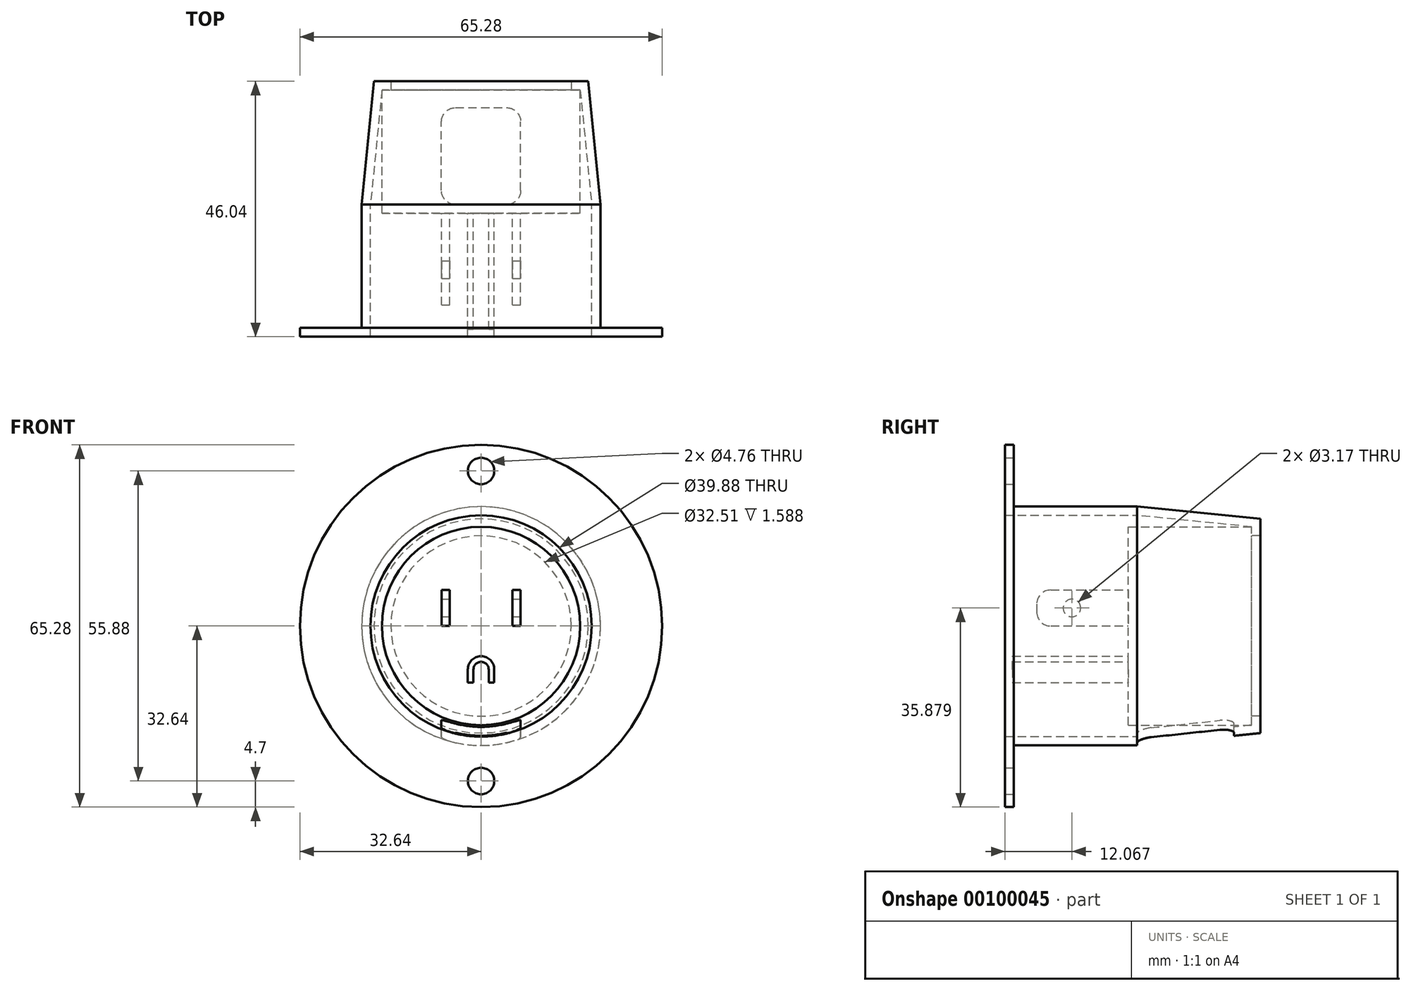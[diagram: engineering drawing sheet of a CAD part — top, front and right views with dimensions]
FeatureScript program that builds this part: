
annotation { "Feature Type Name" : "Feature", "Feature Type Description" : "" }
export const myFeature = defineFeature(function(context is Context, id is Id, definition is map)
    precondition{}
    {
        {
            var Q0;
            Q0=qCreatedBy(makeId("Front.planeOp"),FACE);
            var sketch = newSketch(context, id + "F0", { "sketchPlane" : qUnion([Q0])});
            skCircle(sketch, "E0", {"center": v(0, 0) * mm, "radius": 32.64 * mm});
            skCircle(sketch, "E1", {"center": v(0, 0) * mm, "radius": 19.94 * mm});
            skCircle(sketch, "E2", {"center": v(0, 27.94) * mm, "radius": 2.38 * mm});
            skCircle(sketch, "E3", {"center": v(0, -27.94) * mm, "radius": 2.38 * mm});
            skLineSegment(sketch, "E4", {"start": v(0, 27.94) * mm, "end": v(0, 0) * mm, "construction": true});
            skLineSegment(sketch, "E5", {"start": v(0, 0) * mm, "end": v(0, -27.94) * mm, "construction": true});
            skSolve(sketch);
        }
        {
            var Q0;
            Q0 = qSketchRegion(id + "F0", true);
            extrude(context, id + "F1", {"entities" : qUnion([Q0]), "depth" : 1.59 * mm});
        }
        {
            var Q0;
            Q0=qCreatedBy(makeId("Right.planeOp"),FACE);
            var sketch = newSketch(context, id + "F2", { "sketchPlane" : qUnion([Q0])});
            skLineSegment(sketch, "E6", {"start": v(0, 21.53) * mm, "end": v(22.23, 21.53) * mm});
            skLineSegment(sketch, "E7", {"start": v(22.22, 21.53) * mm, "end": v(44.45, 19.3) * mm});
            skLineSegment(sketch, "E8", {"start": v(44.45, 19.3) * mm, "end": v(44.45, 16.26) * mm});
            skLineSegment(sketch, "E9", {"start": v(42.86, 17.87) * mm, "end": v(22.15, 19.94) * mm});
            skLineSegment(sketch, "E10", {"start": v(22.15, 19.94) * mm, "end": v(0, 19.94) * mm});
            skLineSegment(sketch, "E11", {"start": v(0, 21.53) * mm, "end": v(0, 19.94) * mm});
            skLineSegment(sketch, "E12", {"start": v(0, 0) * mm, "end": v(44.45, 0) * mm, "construction": true});
            skLineSegment(sketch, "E13", {"start": v(11.11, 21.53) * mm, "end": v(11.11, 19.94) * mm, "construction": true});
            skLineSegment(sketch, "E14", {"start": v(42.86, 17.87) * mm, "end": v(43.02, 19.45) * mm, "construction": true});
            skLineSegment(sketch, "E15", {"start": v(42.86, 17.87) * mm, "end": v(42.86, 16.26) * mm});
            skLineSegment(sketch, "E16", {"start": v(42.86, 16.26) * mm, "end": v(44.45, 16.26) * mm});
            skSolve(sketch);
        }
        {
            var Q0;
            Q0 = qSketchRegion(id + "F2", true);
            var Q1;
            Q1=sQuery(id+"F2.wireOp",EDGE,"E12");
            revolve(context, id + "F3", {"operationType" : NewBodyOperationType.ADD, "entities" : qUnion([Q0]), "axis" : qUnion([Q1]), "revolveType" : RevolveType.FULL});
        }
        {
            var Q0;
            Q0=qCreatedBy(makeId("Top.planeOp"),FACE);
            var sketch = newSketch(context, id + "F4", { "sketchPlane" : qUnion([Q0])});
            skLineSegment(sketch, "E17.bottom", {"start": v(-7.14, 22.22) * mm, "end": v(7.14, 22.22) * mm});
            skLineSegment(sketch, "E17.top", {"start": v(-7.14, 39.69) * mm, "end": v(7.14, 39.69) * mm});
            skLineSegment(sketch, "E17.left", {"start": v(-7.14, 22.22) * mm, "end": v(-7.14, 39.69) * mm});
            skLineSegment(sketch, "E17.right", {"start": v(7.14, 22.22) * mm, "end": v(7.14, 39.69) * mm});
            skLineSegment(sketch, "E18", {"start": v(0, 22.22) * mm, "end": v(0, 0) * mm, "construction": true});
            skSolve(sketch);
        }
        {
            var Q0;
            Q0 = qSketchRegion(id + "F4", true);
            extrude(context, id + "F5", {"entities" : qUnion([Q0]), "operationType" : NewBodyOperationType.REMOVE, "oppositeDirection" : true, "depth" : 25.4 * mm});
        }
        {
            var Q0;
            Q0=makeQuery(id+"F5.boolean.opBoolean","COPY",EDGE,{"derivedFrom":makeQuery(id+"F5.opExtrude","SWEPT_EDGE",EDGE,{"disambiguationData":[OSD([sQuery(id+"F4.wireOp",EDGE,"E17.bottom"),sQuery(id+"F4.wireOp",EDGE,"E17.left")])]})});
            var Q1;
            Q1=makeQuery(id+"F5.boolean.opBoolean","COPY",EDGE,{"derivedFrom":makeQuery(id+"F5.opExtrude","SWEPT_EDGE",EDGE,{"disambiguationData":[OSD([sQuery(id+"F4.wireOp",EDGE,"E17.bottom"),sQuery(id+"F4.wireOp",EDGE,"E17.right")])]})});
            var Q2;
            Q2=makeQuery(id+"F5.boolean.opBoolean","COPY",EDGE,{"derivedFrom":makeQuery(id+"F5.opExtrude","SWEPT_EDGE",EDGE,{"disambiguationData":[OSD([sQuery(id+"F4.wireOp",EDGE,"E17.top"),sQuery(id+"F4.wireOp",EDGE,"E17.right")])]})});
            var Q3;
            Q3=makeQuery(id+"F5.boolean.opBoolean","COPY",EDGE,{"derivedFrom":makeQuery(id+"F5.opExtrude","SWEPT_EDGE",EDGE,{"disambiguationData":[OSD([sQuery(id+"F4.wireOp",EDGE,"E17.top"),sQuery(id+"F4.wireOp",EDGE,"E17.left")])]})});
            fillet(context, id + "F6", {"entities" : qUnion([Q0, Q1, Q2, Q3]), "radius" : 2.54 * mm, "tangentPropagation" : true, "allowEdgeOverflow" : false});
        }
        {
            var Q0;
            Q0=makeQuery(id+"F3.opRevolve","SWEPT_FACE",FACE,{"disambiguationData":[OSD([sQuery(id+"F2.wireOp",EDGE,"E15")])]});
            var sketch = newSketch(context, id + "F7", { "sketchPlane" : qUnion([Q0])});
            skCircle(sketch, "E19.0", {"center": v(0, 0) * mm, "radius": 17.87 * mm});
            skSolve(sketch);
        }
        {
            var Q0;
            Q0 = qSketchRegion(id + "F7", true);
            extrude(context, id + "F8", {"entities" : qUnion([Q0]), "operationType" : NewBodyOperationType.ADD, "depth" : 22.22 * mm});
        }
        {
            var Q0;
            Q0=makeQuery(id+"F8.opExtrude","CAP_FACE",FACE,{"disambiguationData":[OSD([sQuery(id+"F7.wireOp",EDGE,"E19.0")])],"isStart":false});
            var sketch = newSketch(context, id + "F9", { "sketchPlane" : qUnion([Q0])});
            skLineSegment(sketch, "E20.bottom", {"start": v(5.64, 6.48) * mm, "end": v(7.14, 6.48) * mm});
            skLineSegment(sketch, "E20.top", {"start": v(5.64, 0) * mm, "end": v(7.14, 0) * mm});
            skLineSegment(sketch, "E20.left", {"start": v(5.64, 6.48) * mm, "end": v(5.64, 0) * mm});
            skLineSegment(sketch, "E20.right", {"start": v(7.14, 6.48) * mm, "end": v(7.14, 0) * mm});
            skLineSegment(sketch, "E21.bottom", {"start": v(-7.14, 6.48) * mm, "end": v(-5.64, 6.48) * mm});
            skLineSegment(sketch, "E21.top", {"start": v(-7.14, 0) * mm, "end": v(-5.64, 0) * mm});
            skLineSegment(sketch, "E21.left", {"start": v(-7.14, 6.48) * mm, "end": v(-7.14, 0) * mm});
            skLineSegment(sketch, "E21.right", {"start": v(-5.64, 6.48) * mm, "end": v(-5.64, 0) * mm});
            skLineSegment(sketch, "E22.top", {"start": v(-2.38, -10.21) * mm, "end": v(-1.37, -10.21) * mm});
            skLineSegment(sketch, "E22.left", {"start": v(-2.38, -7.83) * mm, "end": v(-2.38, -10.21) * mm});
            skLineSegment(sketch, "E22.right", {"start": v(2.38, -7.83) * mm, "end": v(2.38, -10.21) * mm});
            skArc(sketch, "E23", {"start": v(2.38, -7.83) * mm, "mid": v(0, -5.45) * mm, "end": v(-2.38, -7.83) * mm});
            skLineSegment(sketch, "E24", {"start": v(-5.64, 3.24) * mm, "end": v(5.64, 3.24) * mm, "construction": true});
            skLineSegment(sketch, "E25", {"start": v(0, 3.24) * mm, "end": v(0, 0) * mm, "construction": true});
            skLineSegment(sketch, "E26.0", {"start": v(-1.37, -7.83) * mm, "end": v(-1.37, -10.21) * mm});
            skArc(sketch, "E26.1", {"start": v(1.37, -7.83) * mm, "mid": v(0, -6.46) * mm, "end": v(-1.37, -7.83) * mm});
            skLineSegment(sketch, "E26.2", {"start": v(1.37, -7.83) * mm, "end": v(1.37, -10.21) * mm});
            skLineSegment(sketch, "E27.trimOffspring", {"start": v(1.37, -10.21) * mm, "end": v(2.38, -10.21) * mm});
            skSolve(sketch);
        }
        {
            var Q0;
            Q0=makeQuery(id+"F9.imprint","IMPRINT",FACE,{"disambiguationData":[TD([[makeQuery(id+"F9.imprint","IMPRINT",EDGE,{"derivedFrom":sQuery(id+"F9.wireOp",EDGE,"E21.bottom")}),-1.0]])]});
            var Q1;
            Q1=makeQuery(id+"F9.imprint","IMPRINT",FACE,{"disambiguationData":[TD([[makeQuery(id+"F9.imprint","IMPRINT",EDGE,{"derivedFrom":sQuery(id+"F9.wireOp",EDGE,"E20.bottom")}),-1.0]])]});
            extrude(context, id + "F10", {"entities" : qUnion([Q0, Q1]), "operationType" : NewBodyOperationType.ADD, "depth" : 16.5 * mm});
        }
        {
            var Q0;
            Q0=makeQuery(id+"F9.imprint","IMPRINT",FACE,{"disambiguationData":[TD([[makeQuery(id+"F9.imprint","IMPRINT",EDGE,{"derivedFrom":sQuery(id+"F9.wireOp",EDGE,"E22.top")}),1.0]])]});
            extrude(context, id + "F11", {"entities" : qUnion([Q0]), "operationType" : NewBodyOperationType.ADD, "depth" : 20.9 * mm});
        }
        {
            var Q0;
            Q0=makeQuery(id+"F10.opExtrude","CAP_EDGE",EDGE,{"disambiguationData":[OSD([sQuery(id+"F9.wireOp",EDGE,"E21.bottom")])],"isStart":false});
            var Q1;
            Q1=makeQuery(id+"F10.opExtrude","CAP_EDGE",EDGE,{"disambiguationData":[OSD([sQuery(id+"F9.wireOp",EDGE,"E21.top")])],"isStart":false});
            var Q2;
            Q2=makeQuery(id+"F10.opExtrude","CAP_EDGE",EDGE,{"disambiguationData":[OSD([sQuery(id+"F9.wireOp",EDGE,"E20.bottom")])],"isStart":false});
            var Q3;
            Q3=makeQuery(id+"F10.opExtrude","CAP_EDGE",EDGE,{"disambiguationData":[OSD([sQuery(id+"F9.wireOp",EDGE,"E20.top")])],"isStart":false});
            fillet(context, id + "F12", {"entities" : qUnion([Q0, Q1, Q2, Q3]), "radius" : 2.54 * mm, "tangentPropagation" : true, "allowEdgeOverflow" : false});
        }
        {
            var Q0;
            Q0=makeQuery(id+"F10.opExtrude","SWEPT_FACE",FACE,{"disambiguationData":[OSD([sQuery(id+"F9.wireOp",EDGE,"E20.right")])]});
            var sketch = newSketch(context, id + "F13", { "sketchPlane" : qUnion([Q0])});
            skCircle(sketch, "E28", {"center": v(10.48, 3.24) * mm, "radius": 1.59 * mm});
            skLineSegment(sketch, "E29", {"start": v(10.48, 3.24) * mm, "end": v(4.13, 3.24) * mm, "construction": true});
            skPoint(sketch, "E29.endSnap0", {"position": v(4.13, 3.24) * mm});
            skSolve(sketch);
        }
        {
            var Q0;
            Q0 = qSketchRegion(id + "F13", true);
            extrude(context, id + "F14", {"entities" : qUnion([Q0]), "operationType" : NewBodyOperationType.REMOVE, "oppositeDirection" : true, "depth" : 15.24 * mm});
        }
    });
